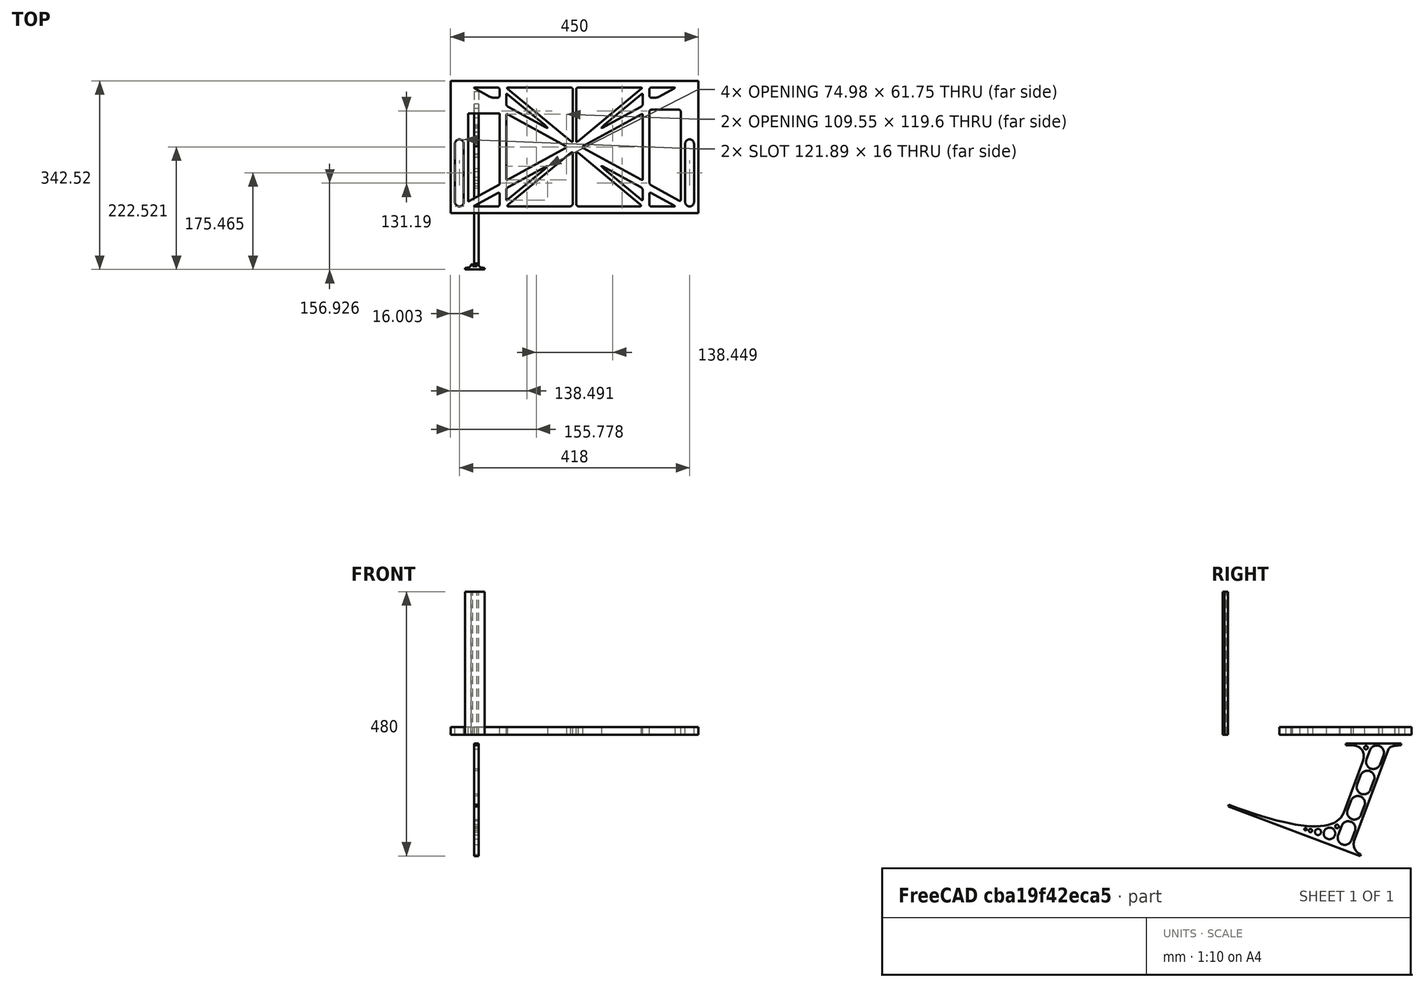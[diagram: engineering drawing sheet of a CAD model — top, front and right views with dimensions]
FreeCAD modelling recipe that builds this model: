
FCSTD DOCUMENT  (FreeCAD 0.19R0.19.2)
Label: laptopStand129FCStd
License: All rights reserved
LicenseURL: http://en.wikipedia.org/wiki/All_rights_reserved
objects: Sketcher::SketchObject×3, Part::Extrusion×3
note: 6 computed .brp shape members not serialized (recipe doc carries the construction recipe); baked Part::Feature solids carry a one-line shape summary decoded from their .brp

FEATURE [Sketcher::SketchObject] Sketch
  FullyConstrained = false
  sketch-geometry (353):
    g0: LineSegment StartX=-10.9272 StartY=-82.7794 StartZ=0 EndX=46.0728 EndY=-51.4823 EndZ=0
    g1: LineSegment StartX=-10.9272 StartY=76.4095 StartZ=0 EndX=-10.9272 EndY=-82.7794 EndZ=0
    g2: LineSegment StartX=46.0728 StartY=76.4095 StartZ=0 EndX=46.0728 EndY=-51.4823 EndZ=0
    g3: LineSegment StartX=-42.9272 StartY=136.221 StartZ=0 EndX=-42.9272 EndY=-103.779 EndZ=0
    g4: LineSegment StartX=407.073 StartY=136.221 StartZ=0 EndX=407.073 EndY=-103.779 EndZ=0
    g5: ArcOfCircle CenterX=-26.9272 CenterY=22.1087 CenterZ=0 NormalX=0 NormalY=0 NormalZ=1 AngleXU=0 Radius=8 StartAngle=1e-16 EndAngle=3.14159
    g6: ArcOfCircle CenterX=-26.9272 CenterY=-83.7794 CenterZ=0 NormalX=0 NormalY=0 NormalZ=1 AngleXU=0 Radius=8 StartAngle=3.14159 EndAngle=6.28319
    g7: LineSegment StartX=-34.9272 StartY=22.1087 StartZ=0 EndX=-34.9272 EndY=-83.7794 EndZ=0
    g8: LineSegment StartX=-18.9272 StartY=22.1087 StartZ=0 EndX=-18.9272 EndY=-83.7794 EndZ=0
    g9: ArcOfCircle CenterX=391.073 CenterY=22.1087 CenterZ=0 NormalX=0 NormalY=0 NormalZ=1 AngleXU=0 Radius=8 StartAngle=-4.4e-15 EndAngle=3.14159
    g10: LineSegment StartX=399.073 StartY=22.1087 StartZ=0 EndX=399.073 EndY=-83.7794 EndZ=0
    g11: LineSegment StartX=383.073 StartY=22.1087 StartZ=0 EndX=383.073 EndY=-83.7794 EndZ=0
    g12: ArcOfCircle CenterX=391.073 CenterY=-83.7794 CenterZ=0 NormalX=0 NormalY=0 NormalZ=1 AngleXU=0 Radius=8 StartAngle=3.14159 EndAngle=6.28319
    g13: Circle CenterX=175.022 CenterY=27.0628 CenterZ=0 NormalX=0 NormalY=0 NormalZ=1 AngleXU=0 Radius=1
    g14: Circle CenterX=179.022 CenterY=24.8665 CenterZ=0 NormalX=0 NormalY=0 NormalZ=1 AngleXU=0 Radius=1
    g15: Circle CenterX=179.022 CenterY=27.0628 CenterZ=0 NormalX=0 NormalY=0 NormalZ=1 AngleXU=0 Radius=1
    g16: BSplineCurve PolesCount=3 KnotsCount=2 Degree=2 IsPeriodic=0
    g17: GeomPoint X=175.022 Y=27.0628 Z=0
    g18: GeomPoint X=179.022 Y=27.0628 Z=0
    g19: Circle CenterX=189.124 CenterY=27.0628 CenterZ=0 NormalX=0 NormalY=0 NormalZ=1 AngleXU=0 Radius=1
    g20: Circle CenterX=185.124 CenterY=24.8665 CenterZ=0 NormalX=0 NormalY=0 NormalZ=1 AngleXU=0 Radius=1
    g21: Circle CenterX=185.124 CenterY=27.0628 CenterZ=0 NormalX=0 NormalY=0 NormalZ=1 AngleXU=0 Radius=1
    g22: BSplineCurve PolesCount=3 KnotsCount=2 Degree=2 IsPeriodic=0
    g23: GeomPoint X=189.124 Y=27.0628 Z=0
    g24: GeomPoint X=185.124 Y=27.0628 Z=0
    g25: Circle CenterX=175.022 CenterY=5.37834 CenterZ=0 NormalX=0 NormalY=0 NormalZ=1 AngleXU=0 Radius=1
    g26: Circle CenterX=179.022 CenterY=7.57463 CenterZ=0 NormalX=0 NormalY=0 NormalZ=1 AngleXU=0 Radius=1
    g27: Circle CenterX=179.022 CenterY=5.34704 CenterZ=0 NormalX=0 NormalY=0 NormalZ=1 AngleXU=0 Radius=1
    g28: BSplineCurve PolesCount=3 KnotsCount=2 Degree=2 IsPeriodic=0
    g29: GeomPoint X=175.022 Y=5.37834 Z=0
    g30: GeomPoint X=179.022 Y=5.34704 Z=0
    g31: Circle CenterX=189.124 CenterY=5.37834 CenterZ=0 NormalX=0 NormalY=0 NormalZ=1 AngleXU=0 Radius=1
    g32: Circle CenterX=185.124 CenterY=7.57463 CenterZ=0 NormalX=0 NormalY=0 NormalZ=1 AngleXU=0 Radius=1
    g33: Circle CenterX=185.124 CenterY=5.34704 CenterZ=0 NormalX=0 NormalY=0 NormalZ=1 AngleXU=0 Radius=1
    g34: BSplineCurve PolesCount=3 KnotsCount=2 Degree=2 IsPeriodic=0
    g35: GeomPoint X=189.124 Y=5.37834 Z=0
    g36: GeomPoint X=185.124 Y=5.34704 Z=0
    g37: Circle CenterX=165.871 CenterY=18.1458 CenterZ=0 NormalX=0 NormalY=0 NormalZ=1 AngleXU=0 Radius=1
    g38: Circle CenterX=169.377 CenterY=16.2206 CenterZ=0 NormalX=0 NormalY=0 NormalZ=1 AngleXU=0 Radius=1
    g39: Circle CenterX=165.871 CenterY=14.2954 CenterZ=0 NormalX=0 NormalY=0 NormalZ=1 AngleXU=0 Radius=1
    g40: BSplineCurve PolesCount=3 KnotsCount=2 Degree=2 IsPeriodic=0
    g41: GeomPoint X=165.871 Y=18.1458 Z=0
    g42: GeomPoint X=165.871 Y=14.2954 Z=0
    g43: Circle CenterX=198.275 CenterY=18.1458 CenterZ=0 NormalX=0 NormalY=0 NormalZ=1 AngleXU=0 Radius=1
    g44: Circle CenterX=194.768 CenterY=16.2206 CenterZ=0 NormalX=0 NormalY=0 NormalZ=1 AngleXU=0 Radius=1
    g45: Circle CenterX=198.275 CenterY=14.2954 CenterZ=0 NormalX=0 NormalY=0 NormalZ=1 AngleXU=0 Radius=1
    g46: BSplineCurve PolesCount=3 KnotsCount=2 Degree=2 IsPeriodic=0
    g47: GeomPoint X=198.275 Y=18.1458 Z=0
    g48: GeomPoint X=198.275 Y=14.2954 Z=0
    g49: LineSegment StartX=407.073 StartY=-103.779 StartZ=0 EndX=-42.9272 EndY=-103.779 EndZ=0
    g50: LineSegment StartX=407.073 StartY=136.221 StartZ=0 EndX=-42.9272 EndY=136.221 EndZ=0
    g51: LineSegment StartX=46.0728 StartY=76.4095 StartZ=0 EndX=-10.9272 EndY=76.4095 EndZ=0
    g52: Circle CenterX=125.607 CenterY=54.1951 CenterZ=0 NormalX=0 NormalY=0 NormalZ=1 AngleXU=0 Radius=1
    g53: Circle CenterX=139.632 CenterY=46.4944 CenterZ=0 NormalX=0 NormalY=0 NormalZ=1 AngleXU=0 Radius=1
    g54: Circle CenterX=127.326 CenterY=56.7187 CenterZ=0 NormalX=0 NormalY=0 NormalZ=1 AngleXU=0 Radius=1
    g55: BSplineCurve PolesCount=3 KnotsCount=2 Degree=2 IsPeriodic=0
    g56: GeomPoint X=125.607 Y=54.1951 Z=0
    g57: GeomPoint X=127.326 Y=56.7187 Z=0
    g58: Circle CenterX=236.821 CenterY=56.7187 CenterZ=0 NormalX=0 NormalY=0 NormalZ=1 AngleXU=0 Radius=1
    g59: Circle CenterX=224.513 CenterY=46.4944 CenterZ=0 NormalX=0 NormalY=0 NormalZ=1 AngleXU=0 Radius=1
    g60: Circle CenterX=238.538 CenterY=54.1951 CenterZ=0 NormalX=0 NormalY=0 NormalZ=1 AngleXU=0 Radius=1
    g61: BSplineCurve PolesCount=3 KnotsCount=2 Degree=2 IsPeriodic=0
    g62: GeomPoint X=236.821 Y=56.7187 Z=0
    g63: GeomPoint X=238.538 Y=54.1951 Z=0
    g64: Circle CenterX=238.538 CenterY=-21.7539 CenterZ=0 NormalX=0 NormalY=0 NormalZ=1 AngleXU=0 Radius=1
    g65: Circle CenterX=224.513 CenterY=-14.0532 CenterZ=0 NormalX=0 NormalY=0 NormalZ=1 AngleXU=0 Radius=1
    g66: Circle CenterX=236.821 CenterY=-24.2775 CenterZ=0 NormalX=0 NormalY=0 NormalZ=1 AngleXU=0 Radius=1
    g67: BSplineCurve PolesCount=3 KnotsCount=2 Degree=2 IsPeriodic=0
    g68: GeomPoint X=238.538 Y=-21.7539 Z=0
    g69: GeomPoint X=236.821 Y=-24.2775 Z=0
    g70: Circle CenterX=125.607 CenterY=-21.7539 CenterZ=0 NormalX=0 NormalY=0 NormalZ=1 AngleXU=0 Radius=1
    g71: Circle CenterX=139.632 CenterY=-14.0532 CenterZ=0 NormalX=0 NormalY=0 NormalZ=1 AngleXU=0 Radius=1
    g72: Circle CenterX=127.325 CenterY=-24.2775 CenterZ=0 NormalX=0 NormalY=0 NormalZ=1 AngleXU=0 Radius=1
    g73: BSplineCurve PolesCount=3 KnotsCount=2 Degree=2 IsPeriodic=0
    g74: GeomPoint X=125.607 Y=-21.7539 Z=0
    g75: GeomPoint X=127.325 Y=-24.2775 Z=0
    g76: Circle CenterX=302.996 CenterY=111.695 CenterZ=0 NormalX=0 NormalY=0 NormalZ=1 AngleXU=0 Radius=1
    g77: Circle CenterX=306.073 CenterY=114.251 CenterZ=0 NormalX=0 NormalY=0 NormalZ=1 AngleXU=0 Radius=1
    g78: Circle CenterX=306.073 CenterY=110.251 CenterZ=0 NormalX=0 NormalY=0 NormalZ=1 AngleXU=0 Radius=1
    g79: BSplineCurve PolesCount=3 KnotsCount=2 Degree=2 IsPeriodic=0
    g80: GeomPoint X=302.996 Y=111.695 Z=0
    g81: GeomPoint X=306.073 Y=110.251 Z=0
    g82: Circle CenterX=306.073 CenterY=95.2763 CenterZ=0 NormalX=0 NormalY=0 NormalZ=1 AngleXU=0 Radius=1
    g83: Circle CenterX=306.073 CenterY=91.2763 CenterZ=0 NormalX=0 NormalY=0 NormalZ=1 AngleXU=0 Radius=1
    g84: Circle CenterX=302.567 CenterY=89.3511 CenterZ=0 NormalX=0 NormalY=0 NormalZ=1 AngleXU=0 Radius=1
    g85: BSplineCurve PolesCount=3 KnotsCount=2 Degree=2 IsPeriodic=0
    g86: GeomPoint X=306.073 Y=95.2763 Z=0
    g87: GeomPoint X=302.567 Y=89.3511 Z=0
    g88: LineSegment StartX=306.073 StartY=110.251 StartZ=0 EndX=306.073 EndY=95.2763 EndZ=0
    g89: LineSegment StartX=302.996 StartY=111.695 StartZ=0 EndX=236.821 EndY=56.7187 EndZ=0
    g90: LineSegment StartX=238.538 StartY=54.1951 StartZ=0 EndX=302.567 EndY=89.3511 EndZ=0
    g91: Circle CenterX=61.1496 CenterY=111.695 CenterZ=0 NormalX=0 NormalY=0 NormalZ=1 AngleXU=0 Radius=1
    g92: Circle CenterX=58.0728 CenterY=114.251 CenterZ=0 NormalX=0 NormalY=0 NormalZ=1 AngleXU=0 Radius=1
    g93: Circle CenterX=58.0728 CenterY=110.251 CenterZ=0 NormalX=0 NormalY=0 NormalZ=1 AngleXU=0 Radius=1
    g94: BSplineCurve PolesCount=3 KnotsCount=2 Degree=2 IsPeriodic=0
    g95: GeomPoint X=61.1496 Y=111.695 Z=0
    g96: GeomPoint X=58.0728 Y=110.251 Z=0
    g97: Circle CenterX=61.5791 CenterY=89.3511 CenterZ=0 NormalX=0 NormalY=0 NormalZ=1 AngleXU=0 Radius=1
    g98: Circle CenterX=58.0728 CenterY=91.2763 CenterZ=0 NormalX=0 NormalY=0 NormalZ=1 AngleXU=0 Radius=1
    g99: Circle CenterX=58.0728 CenterY=95.2763 CenterZ=0 NormalX=0 NormalY=0 NormalZ=1 AngleXU=0 Radius=1
    g100: BSplineCurve PolesCount=3 KnotsCount=2 Degree=2 IsPeriodic=0
    g101: GeomPoint X=61.5791 Y=89.3511 Z=0
    g102: GeomPoint X=58.0728 Y=95.2763 Z=0
    g103: LineSegment StartX=58.0728 StartY=110.251 StartZ=0 EndX=58.0728 EndY=95.2763 EndZ=0
    g104: LineSegment StartX=61.1496 StartY=111.695 StartZ=0 EndX=127.326 EndY=56.7187 EndZ=0
    g105: LineSegment StartX=125.607 StartY=54.1951 StartZ=0 EndX=61.5791 EndY=89.3511 EndZ=0
    g106: Circle CenterX=61.5791 CenterY=-56.9099 CenterZ=0 NormalX=0 NormalY=0 NormalZ=1 AngleXU=0 Radius=1
    g107: Circle CenterX=58.0728 CenterY=-58.8351 CenterZ=0 NormalX=0 NormalY=0 NormalZ=1 AngleXU=0 Radius=1
    g108: Circle CenterX=58.0728 CenterY=-62.8351 CenterZ=0 NormalX=0 NormalY=0 NormalZ=1 AngleXU=0 Radius=1
    g109: BSplineCurve PolesCount=3 KnotsCount=2 Degree=2 IsPeriodic=0
    g110: GeomPoint X=61.5791 Y=-56.9099 Z=0
    g111: GeomPoint X=58.0728 Y=-62.8351 Z=0
    g112: Circle CenterX=58.0728 CenterY=-77.8102 CenterZ=0 NormalX=0 NormalY=0 NormalZ=1 AngleXU=0 Radius=1
    g113: Circle CenterX=58.0728 CenterY=-81.8102 CenterZ=0 NormalX=0 NormalY=0 NormalZ=1 AngleXU=0 Radius=1
    g114: Circle CenterX=61.1496 CenterY=-79.2541 CenterZ=0 NormalX=0 NormalY=0 NormalZ=1 AngleXU=0 Radius=1
    g115: BSplineCurve PolesCount=3 KnotsCount=2 Degree=2 IsPeriodic=0
    g116: GeomPoint X=58.0728 Y=-77.8102 Z=0
    g117: GeomPoint X=61.1496 Y=-79.2541 Z=0
    g118: LineSegment StartX=58.0728 StartY=-62.8351 StartZ=0 EndX=58.0728 EndY=-77.8102 EndZ=0
    g119: LineSegment StartX=61.1496 StartY=-79.2541 StartZ=0 EndX=127.325 EndY=-24.2775 EndZ=0
    g120: LineSegment StartX=125.607 StartY=-21.7539 StartZ=0 EndX=61.5791 EndY=-56.9099 EndZ=0
    g121: Circle CenterX=302.567 CenterY=-56.9099 CenterZ=0 NormalX=0 NormalY=0 NormalZ=1 AngleXU=0 Radius=1
    g122: Circle CenterX=306.073 CenterY=-58.8351 CenterZ=0 NormalX=0 NormalY=0 NormalZ=1 AngleXU=0 Radius=1
    g123: Circle CenterX=306.073 CenterY=-62.8351 CenterZ=0 NormalX=0 NormalY=0 NormalZ=1 AngleXU=0 Radius=1
    g124: BSplineCurve PolesCount=3 KnotsCount=2 Degree=2 IsPeriodic=0
    g125: GeomPoint X=302.567 Y=-56.9099 Z=0
    g126: GeomPoint X=306.073 Y=-62.8351 Z=0
    g127: Circle CenterX=302.996 CenterY=-79.2541 CenterZ=0 NormalX=0 NormalY=0 NormalZ=1 AngleXU=0 Radius=1
    g128: Circle CenterX=306.073 CenterY=-81.8102 CenterZ=0 NormalX=0 NormalY=0 NormalZ=1 AngleXU=0 Radius=1
    g129: Circle CenterX=306.073 CenterY=-77.8102 CenterZ=0 NormalX=0 NormalY=0 NormalZ=1 AngleXU=0 Radius=1
    g130: BSplineCurve PolesCount=3 KnotsCount=2 Degree=2 IsPeriodic=0
    g131: GeomPoint X=302.996 Y=-79.2541 Z=0
    g132: GeomPoint X=306.073 Y=-77.8102 Z=0
    g133: LineSegment StartX=306.073 StartY=-62.8351 StartZ=0 EndX=306.073 EndY=-77.8102 EndZ=0
    g134: LineSegment StartX=302.996 StartY=-79.2541 StartZ=0 EndX=236.821 EndY=-24.2775 EndZ=0
    g135: LineSegment StartX=238.538 StartY=-21.7539 StartZ=0 EndX=302.567 EndY=-56.9099 EndZ=0
    g136: Circle CenterX=61.6457 CenterY=-88.8112 CenterZ=0 NormalX=0 NormalY=0 NormalZ=1 AngleXU=0 Radius=1
    g137: Circle CenterX=58.0728 CenterY=-91.7794 CenterZ=0 NormalX=0 NormalY=0 NormalZ=1 AngleXU=0 Radius=1
    g138: Circle CenterX=63.9135 CenterY=-91.7794 CenterZ=0 NormalX=0 NormalY=0 NormalZ=1 AngleXU=0 Radius=1
    g139: BSplineCurve PolesCount=3 KnotsCount=2 Degree=2 IsPeriodic=0
    g140: GeomPoint X=61.6457 Y=-88.8112 Z=0
    g141: GeomPoint X=63.9135 Y=-91.7794 Z=0
    g142: Circle CenterX=179.022 CenterY=-85.8163 CenterZ=0 NormalX=0 NormalY=0 NormalZ=1 AngleXU=0 Radius=1
    g143: Circle CenterX=179.022 CenterY=-91.7794 CenterZ=0 NormalX=0 NormalY=0 NormalZ=1 AngleXU=0 Radius=1
    g144: Circle CenterX=171.895 CenterY=-91.7794 CenterZ=0 NormalX=0 NormalY=0 NormalZ=1 AngleXU=0 Radius=1
    g145: BSplineCurve PolesCount=3 KnotsCount=2 Degree=2 IsPeriodic=0
    g146: GeomPoint X=179.022 Y=-85.8163 Z=0
    g147: GeomPoint X=171.895 Y=-91.7794 Z=0
    g148: Circle CenterX=185.124 CenterY=-86.2028 CenterZ=0 NormalX=0 NormalY=0 NormalZ=1 AngleXU=0 Radius=1
    g149: Circle CenterX=185.124 CenterY=-91.7794 CenterZ=0 NormalX=0 NormalY=0 NormalZ=1 AngleXU=0 Radius=1
    g150: Circle CenterX=191.747 CenterY=-91.7794 CenterZ=0 NormalX=0 NormalY=0 NormalZ=1 AngleXU=0 Radius=1
    g151: BSplineCurve PolesCount=3 KnotsCount=2 Degree=2 IsPeriodic=0
    g152: GeomPoint X=185.124 Y=-86.2028 Z=0
    g153: GeomPoint X=191.747 Y=-91.7794 Z=0
    g154: Circle CenterX=299.888 CenterY=-86.6413 CenterZ=0 NormalX=0 NormalY=0 NormalZ=1 AngleXU=0 Radius=1
    g155: Circle CenterX=306.073 CenterY=-91.7794 CenterZ=0 NormalX=0 NormalY=0 NormalZ=1 AngleXU=0 Radius=1
    g156: Circle CenterX=298.776 CenterY=-91.7794 CenterZ=0 NormalX=0 NormalY=0 NormalZ=1 AngleXU=0 Radius=1
    g157: BSplineCurve PolesCount=3 KnotsCount=2 Degree=2 IsPeriodic=0
    g158: GeomPoint X=299.888 Y=-86.6413 Z=0
    g159: GeomPoint X=298.776 Y=-91.7794 Z=0
    g160: LineSegment StartX=189.124 StartY=5.37834 StartZ=0 EndX=299.888 EndY=-86.6413 EndZ=0
    g161: LineSegment StartX=298.776 StartY=-91.7794 StartZ=0 EndX=191.747 EndY=-91.7794 EndZ=0
    g162: LineSegment StartX=185.124 StartY=-86.2028 StartZ=0 EndX=185.124 EndY=5.34704 EndZ=0
    g163: LineSegment StartX=179.022 StartY=5.34704 StartZ=0 EndX=179.022 EndY=-85.8163 EndZ=0
    g164: LineSegment StartX=171.895 StartY=-91.7794 StartZ=0 EndX=63.9135 EndY=-91.7794 EndZ=0
    g165: LineSegment StartX=61.6457 StartY=-88.8112 StartZ=0 EndX=175.022 EndY=5.37834 EndZ=0
    g166: Circle CenterX=302.073 CenterY=124.221 CenterZ=0 NormalX=0 NormalY=0 NormalZ=1 AngleXU=0 Radius=1
    g167: Circle CenterX=306.073 CenterY=124.221 CenterZ=0 NormalX=0 NormalY=0 NormalZ=1 AngleXU=0 Radius=1
    g168: Circle CenterX=302.996 CenterY=121.665 CenterZ=0 NormalX=0 NormalY=0 NormalZ=1 AngleXU=0 Radius=1
    g169: BSplineCurve PolesCount=3 KnotsCount=2 Degree=2 IsPeriodic=0
    g170: GeomPoint X=302.073 Y=124.221 Z=0
    g171: GeomPoint X=302.996 Y=121.665 Z=0
    g172: Circle CenterX=189.124 CenterY=124.221 CenterZ=0 NormalX=0 NormalY=0 NormalZ=1 AngleXU=0 Radius=1
    g173: Circle CenterX=185.124 CenterY=124.221 CenterZ=0 NormalX=0 NormalY=0 NormalZ=1 AngleXU=0 Radius=1
    g174: Circle CenterX=185.124 CenterY=120.221 CenterZ=0 NormalX=0 NormalY=0 NormalZ=1 AngleXU=0 Radius=1
    g175: BSplineCurve PolesCount=3 KnotsCount=2 Degree=2 IsPeriodic=0
    g176: GeomPoint X=189.124 Y=124.221 Z=0
    g177: GeomPoint X=185.124 Y=120.221 Z=0
    g178: Circle CenterX=175.022 CenterY=124.221 CenterZ=0 NormalX=0 NormalY=0 NormalZ=1 AngleXU=0 Radius=1
    g179: Circle CenterX=179.022 CenterY=124.221 CenterZ=0 NormalX=0 NormalY=0 NormalZ=1 AngleXU=0 Radius=1
    g180: Circle CenterX=179.022 CenterY=120.221 CenterZ=0 NormalX=0 NormalY=0 NormalZ=1 AngleXU=0 Radius=1
    g181: BSplineCurve PolesCount=3 KnotsCount=2 Degree=2 IsPeriodic=0
    g182: GeomPoint X=175.022 Y=124.221 Z=0
    g183: GeomPoint X=179.022 Y=120.221 Z=0
    g184: Circle CenterX=62.0728 CenterY=124.221 CenterZ=0 NormalX=0 NormalY=0 NormalZ=1 AngleXU=0 Radius=1
    g185: Circle CenterX=58.0728 CenterY=124.221 CenterZ=0 NormalX=0 NormalY=0 NormalZ=1 AngleXU=0 Radius=1
    g186: Circle CenterX=61.1496 CenterY=121.665 CenterZ=0 NormalX=0 NormalY=0 NormalZ=1 AngleXU=0 Radius=1
    g187: BSplineCurve PolesCount=3 KnotsCount=2 Degree=2 IsPeriodic=0
    g188: GeomPoint X=62.0728 Y=124.221 Z=0
    g189: GeomPoint X=61.1496 Y=121.665 Z=0
    g190: LineSegment StartX=62.0728 StartY=124.221 StartZ=0 EndX=175.022 EndY=124.221 EndZ=0
    g191: LineSegment StartX=179.022 StartY=120.221 StartZ=0 EndX=179.022 EndY=27.0628 EndZ=0
    g192: LineSegment StartX=185.124 StartY=27.0628 StartZ=0 EndX=185.124 EndY=120.221 EndZ=0
    g193: LineSegment StartX=189.124 StartY=124.221 StartZ=0 EndX=302.073 EndY=124.221 EndZ=0
    g194: LineSegment StartX=302.996 StartY=121.665 StartZ=0 EndX=189.124 EndY=27.0628 EndZ=0
    g195: LineSegment StartX=175.022 StartY=27.0628 StartZ=0 EndX=61.1496 EndY=121.665 EndZ=0
    g196: Circle CenterX=61.5791 CenterY=75.4095 CenterZ=0 NormalX=0 NormalY=0 NormalZ=1 AngleXU=0 Radius=1
    g197: Circle CenterX=58.0728 CenterY=77.3346 CenterZ=0 NormalX=0 NormalY=0 NormalZ=1 AngleXU=0 Radius=1
    g198: Circle CenterX=58.0728 CenterY=73.3346 CenterZ=0 NormalX=0 NormalY=0 NormalZ=1 AngleXU=0 Radius=1
    g199: BSplineCurve PolesCount=3 KnotsCount=2 Degree=2 IsPeriodic=0
    g200: GeomPoint X=61.5791 Y=75.4095 Z=0
    g201: GeomPoint X=58.0728 Y=73.3346 Z=0
    g202: Circle CenterX=58.0728 CenterY=-40.8935 CenterZ=0 NormalX=0 NormalY=0 NormalZ=1 AngleXU=0 Radius=1
    g203: Circle CenterX=58.0728 CenterY=-44.8935 CenterZ=0 NormalX=0 NormalY=0 NormalZ=1 AngleXU=0 Radius=1
    g204: Circle CenterX=61.5791 CenterY=-42.9683 CenterZ=0 NormalX=0 NormalY=0 NormalZ=1 AngleXU=0 Radius=1
    g205: BSplineCurve PolesCount=3 KnotsCount=2 Degree=2 IsPeriodic=0
    g206: GeomPoint X=58.0728 Y=-40.8935 Z=0
    g207: GeomPoint X=61.5791 Y=-42.9683 Z=0
    g208: LineSegment StartX=61.5791 StartY=-42.9683 StartZ=0 EndX=165.871 EndY=14.2954 EndZ=0
    g209: LineSegment StartX=165.871 StartY=18.1458 StartZ=0 EndX=61.5791 EndY=75.4095 EndZ=0
    g210: LineSegment StartX=58.0728 StartY=73.3346 StartZ=0 EndX=58.0728 EndY=-40.8935 EndZ=0
    g211: Circle CenterX=302.567 CenterY=-42.9683 CenterZ=0 NormalX=0 NormalY=0 NormalZ=1 AngleXU=0 Radius=1
    g212: Circle CenterX=306.073 CenterY=-44.8935 CenterZ=0 NormalX=0 NormalY=0 NormalZ=1 AngleXU=0 Radius=1
    g213: Circle CenterX=306.073 CenterY=-40.8935 CenterZ=0 NormalX=0 NormalY=0 NormalZ=1 AngleXU=0 Radius=1
    g214: BSplineCurve PolesCount=3 KnotsCount=2 Degree=2 IsPeriodic=0
    g215: GeomPoint X=302.567 Y=-42.9683 Z=0
    g216: GeomPoint X=306.073 Y=-40.8935 Z=0
    g217: Circle CenterX=306.073 CenterY=73.3346 CenterZ=0 NormalX=0 NormalY=0 NormalZ=1 AngleXU=0 Radius=1
    g218: Circle CenterX=306.073 CenterY=77.3346 CenterZ=0 NormalX=0 NormalY=0 NormalZ=1 AngleXU=0 Radius=1
    g219: Circle CenterX=302.567 CenterY=75.4095 CenterZ=0 NormalX=0 NormalY=0 NormalZ=1 AngleXU=0 Radius=1
    g220: BSplineCurve PolesCount=3 KnotsCount=2 Degree=2 IsPeriodic=0
    g221: GeomPoint X=306.073 Y=73.3346 Z=0
    g222: GeomPoint X=302.567 Y=75.4095 Z=0
    g223: LineSegment StartX=302.567 StartY=-42.9683 StartZ=0 EndX=198.275 EndY=14.2954 EndZ=0
    g224: LineSegment StartX=198.275 StartY=18.1458 StartZ=0 EndX=302.567 EndY=75.4095 EndZ=0
    g225: LineSegment StartX=306.073 StartY=73.3346 StartZ=0 EndX=306.073 EndY=-40.8935 EndZ=0
    g226: LineSegment StartX=322.073 StartY=105.865 StartZ=0 EndX=328.643 EndY=105.865 EndZ=0
    g227: LineSegment StartX=318.073 StartY=120.221 StartZ=0 EndX=318.073 EndY=109.865 EndZ=0
    g228: LineSegment StartX=336.157 StartY=107.779 StartZ=0 EndX=362.567 EndY=122.294 EndZ=0
    g229: Circle CenterX=362.073 CenterY=124.221 CenterZ=0 NormalX=0 NormalY=0 NormalZ=1 AngleXU=0 Radius=1
    g230: Circle CenterX=366.073 CenterY=124.221 CenterZ=0 NormalX=0 NormalY=0 NormalZ=1 AngleXU=0 Radius=1
    g231: Circle CenterX=362.567 CenterY=122.294 CenterZ=0 NormalX=0 NormalY=0 NormalZ=1 AngleXU=0 Radius=1
    g232: BSplineCurve PolesCount=3 KnotsCount=2 Degree=2 IsPeriodic=0
    g233: GeomPoint X=362.073 Y=124.221 Z=0
    g234: GeomPoint X=362.567 Y=122.294 Z=0
    g235: Circle CenterX=322.073 CenterY=124.221 CenterZ=0 NormalX=0 NormalY=0 NormalZ=1 AngleXU=0 Radius=1
    g236: Circle CenterX=318.073 CenterY=124.221 CenterZ=0 NormalX=0 NormalY=0 NormalZ=1 AngleXU=0 Radius=1
    g237: Circle CenterX=318.073 CenterY=120.221 CenterZ=0 NormalX=0 NormalY=0 NormalZ=1 AngleXU=0 Radius=1
    g238: BSplineCurve PolesCount=3 KnotsCount=2 Degree=2 IsPeriodic=0
    g239: GeomPoint X=322.073 Y=124.221 Z=0
    g240: GeomPoint X=318.073 Y=120.221 Z=0
    g241: Circle CenterX=322.073 CenterY=105.865 CenterZ=0 NormalX=0 NormalY=0 NormalZ=1 AngleXU=0 Radius=1
    g242: Circle CenterX=318.073 CenterY=105.865 CenterZ=0 NormalX=0 NormalY=0 NormalZ=1 AngleXU=0 Radius=1
    g243: Circle CenterX=318.073 CenterY=109.865 CenterZ=0 NormalX=0 NormalY=0 NormalZ=1 AngleXU=0 Radius=1
    g244: BSplineCurve PolesCount=3 KnotsCount=2 Degree=2 IsPeriodic=0
    g245: GeomPoint X=322.073 Y=105.865 Z=0
    g246: GeomPoint X=318.073 Y=109.865 Z=0
    g247: Circle CenterX=336.157 CenterY=107.779 CenterZ=0 NormalX=0 NormalY=0 NormalZ=1 AngleXU=0 Radius=1
    g248: Circle CenterX=332.651 CenterY=105.853 CenterZ=0 NormalX=0 NormalY=0 NormalZ=1 AngleXU=0 Radius=1
    g249: Circle CenterX=328.643 CenterY=105.865 CenterZ=0 NormalX=0 NormalY=0 NormalZ=1 AngleXU=0 Radius=1
    g250: BSplineCurve PolesCount=3 KnotsCount=2 Degree=2 IsPeriodic=0
    g251: GeomPoint X=336.157 Y=107.779 Z=0
    g252: GeomPoint X=328.643 Y=105.865 Z=0
    g253: LineSegment StartX=322.073 StartY=124.221 StartZ=0 EndX=362.073 EndY=124.221 EndZ=0
    g254: Circle CenterX=371.567 CenterY=-80.8644 CenterZ=0 NormalX=0 NormalY=0 NormalZ=1 AngleXU=0 Radius=1
    g255: Circle CenterX=375.073 CenterY=-82.7896 CenterZ=0 NormalX=0 NormalY=0 NormalZ=1 AngleXU=0 Radius=1
    g256: Circle CenterX=375.073 CenterY=-78.7896 CenterZ=0 NormalX=0 NormalY=0 NormalZ=1 AngleXU=0 Radius=1
    g257: BSplineCurve PolesCount=3 KnotsCount=2 Degree=2 IsPeriodic=0
    g258: GeomPoint X=371.567 Y=-80.8644 Z=0
    g259: GeomPoint X=375.073 Y=-78.7896 Z=0
    g260: Circle CenterX=321.579 CenterY=-53.4075 CenterZ=0 NormalX=0 NormalY=0 NormalZ=1 AngleXU=0 Radius=1
    g261: Circle CenterX=318.073 CenterY=-51.4823 CenterZ=0 NormalX=0 NormalY=0 NormalZ=1 AngleXU=0 Radius=1
    g262: Circle CenterX=318.073 CenterY=-47.4823 CenterZ=0 NormalX=0 NormalY=0 NormalZ=1 AngleXU=0 Radius=1
    g263: BSplineCurve PolesCount=3 KnotsCount=2 Degree=2 IsPeriodic=0
    g264: GeomPoint X=321.579 Y=-53.4075 Z=0
    g265: GeomPoint X=318.073 Y=-47.4823 Z=0
    g266: Circle CenterX=318.073 CenterY=79.9235 CenterZ=0 NormalX=0 NormalY=0 NormalZ=1 AngleXU=0 Radius=1
    g267: Circle CenterX=318.073 CenterY=83.9235 CenterZ=0 NormalX=0 NormalY=0 NormalZ=1 AngleXU=0 Radius=1
    g268: Circle CenterX=322.073 CenterY=83.9235 CenterZ=0 NormalX=0 NormalY=0 NormalZ=1 AngleXU=0 Radius=1
    g269: BSplineCurve PolesCount=3 KnotsCount=2 Degree=2 IsPeriodic=0
    g270: GeomPoint X=318.073 Y=79.9235 Z=0
    g271: GeomPoint X=322.073 Y=83.9235 Z=0
    g272: Circle CenterX=375.073 CenterY=79.9235 CenterZ=0 NormalX=0 NormalY=0 NormalZ=1 AngleXU=0 Radius=1
    g273: Circle CenterX=375.073 CenterY=83.9235 CenterZ=0 NormalX=0 NormalY=0 NormalZ=1 AngleXU=0 Radius=1
    g274: Circle CenterX=371.073 CenterY=83.9235 CenterZ=0 NormalX=0 NormalY=0 NormalZ=1 AngleXU=0 Radius=1
    g275: BSplineCurve PolesCount=3 KnotsCount=2 Degree=2 IsPeriodic=0
    g276: GeomPoint X=375.073 Y=79.9235 Z=0
    g277: GeomPoint X=371.073 Y=83.9235 Z=0
    g278: LineSegment StartX=375.073 StartY=79.9235 StartZ=0 EndX=375.073 EndY=78.9235 EndZ=0
    g279: LineSegment StartX=371.567 StartY=-80.8644 StartZ=0 EndX=321.579 EndY=-53.4075 EndZ=0
    g280: LineSegment StartX=318.073 StartY=-47.4823 StartZ=0 EndX=318.073 EndY=76.4095 EndZ=0
    g281: Circle CenterX=321.579 CenterY=-67.3492 CenterZ=0 NormalX=0 NormalY=0 NormalZ=1 AngleXU=0 Radius=1
    g282: Circle CenterX=318.073 CenterY=-65.424 CenterZ=0 NormalX=0 NormalY=0 NormalZ=1 AngleXU=0 Radius=1
    g283: Circle CenterX=318.073 CenterY=-69.424 CenterZ=0 NormalX=0 NormalY=0 NormalZ=1 AngleXU=0 Radius=1
    g284: BSplineCurve PolesCount=3 KnotsCount=2 Degree=2 IsPeriodic=0
    g285: GeomPoint X=321.579 Y=-67.3492 Z=0
    g286: GeomPoint X=318.073 Y=-69.424 Z=0
    g287: Circle CenterX=362.567 CenterY=-89.8542 CenterZ=0 NormalX=0 NormalY=0 NormalZ=1 AngleXU=0 Radius=1
    g288: Circle CenterX=366.073 CenterY=-91.7794 CenterZ=0 NormalX=0 NormalY=0 NormalZ=1 AngleXU=0 Radius=1
    g289: Circle CenterX=362.073 CenterY=-91.7794 CenterZ=0 NormalX=0 NormalY=0 NormalZ=1 AngleXU=0 Radius=1
    g290: BSplineCurve PolesCount=3 KnotsCount=2 Degree=2 IsPeriodic=0
    g291: GeomPoint X=362.567 Y=-89.8542 Z=0
    g292: GeomPoint X=362.073 Y=-91.7794 Z=0
    g293: Circle CenterX=322.073 CenterY=-91.7794 CenterZ=0 NormalX=0 NormalY=0 NormalZ=1 AngleXU=0 Radius=1
    g294: Circle CenterX=318.073 CenterY=-91.7794 CenterZ=0 NormalX=0 NormalY=0 NormalZ=1 AngleXU=0 Radius=1
    g295: Circle CenterX=318.073 CenterY=-87.7794 CenterZ=0 NormalX=0 NormalY=0 NormalZ=1 AngleXU=0 Radius=1
    g296: BSplineCurve PolesCount=3 KnotsCount=2 Degree=2 IsPeriodic=0
    g297: GeomPoint X=322.073 Y=-91.7794 Z=0
    g298: GeomPoint X=318.073 Y=-87.7794 Z=0
    g299: LineSegment StartX=362.567 StartY=-89.8542 StartZ=0 EndX=321.579 EndY=-67.3492 EndZ=0
    g300: LineSegment StartX=318.073 StartY=-69.424 StartZ=0 EndX=318.073 EndY=-87.7794 EndZ=0
    g301: LineSegment StartX=322.073 StartY=-91.7794 StartZ=0 EndX=362.073 EndY=-91.7794 EndZ=0
    g302: Circle CenterX=2.07281 CenterY=124.221 CenterZ=0 NormalX=0 NormalY=0 NormalZ=1 AngleXU=0 Radius=1
    g303: Circle CenterX=1.57905 CenterY=122.295 CenterZ=0 NormalX=0 NormalY=0 NormalZ=1 AngleXU=0 Radius=1
    g304: BSplineCurve PolesCount=3 KnotsCount=2 Degree=2 IsPeriodic=0
    g305: GeomPoint X=2.07281 Y=124.221 Z=0
    g306: GeomPoint X=1.57905 Y=122.295 Z=0
    g307: Circle CenterX=42.0728 CenterY=124.221 CenterZ=0 NormalX=0 NormalY=0 NormalZ=1 AngleXU=0 Radius=1
    g308: Circle CenterX=46.0728 CenterY=124.221 CenterZ=0 NormalX=0 NormalY=0 NormalZ=1 AngleXU=0 Radius=1
    g309: Circle CenterX=46.0728 CenterY=120.221 CenterZ=0 NormalX=0 NormalY=0 NormalZ=1 AngleXU=0 Radius=1
    g310: BSplineCurve PolesCount=3 KnotsCount=2 Degree=2 IsPeriodic=0
    g311: GeomPoint X=42.0728 Y=124.221 Z=0
    g312: GeomPoint X=46.0728 Y=120.221 Z=0
    g313: Circle CenterX=46.0728 CenterY=109.865 CenterZ=0 NormalX=0 NormalY=0 NormalZ=1 AngleXU=0 Radius=1
    g314: Circle CenterX=46.0728 CenterY=105.865 CenterZ=0 NormalX=0 NormalY=0 NormalZ=1 AngleXU=0 Radius=1
    g315: Circle CenterX=42.0728 CenterY=105.865 CenterZ=0 NormalX=0 NormalY=0 NormalZ=1 AngleXU=0 Radius=1
    g316: BSplineCurve PolesCount=3 KnotsCount=2 Degree=2 IsPeriodic=0
    g317: GeomPoint X=46.0728 Y=109.865 Z=0
    g318: GeomPoint X=42.0728 Y=105.865 Z=0
    g319: Circle CenterX=35.5028 CenterY=105.865 CenterZ=0 NormalX=0 NormalY=0 NormalZ=1 AngleXU=0 Radius=1
    g320: Circle CenterX=31.5028 CenterY=105.865 CenterZ=0 NormalX=0 NormalY=0 NormalZ=1 AngleXU=0 Radius=1
    g321: Circle CenterX=27.9965 CenterY=107.79 CenterZ=0 NormalX=0 NormalY=0 NormalZ=1 AngleXU=0 Radius=1
    g322: BSplineCurve PolesCount=3 KnotsCount=2 Degree=2 IsPeriodic=0
    g323: GeomPoint X=35.5028 Y=105.865 Z=0
    g324: GeomPoint X=27.9965 Y=107.79 Z=0
    g325: LineSegment StartX=2.07281 StartY=124.221 StartZ=0 EndX=42.0728 EndY=124.221 EndZ=0
    g326: LineSegment StartX=46.0728 StartY=120.221 StartZ=0 EndX=46.0728 EndY=109.865 EndZ=0
    g327: LineSegment StartX=42.0728 StartY=105.865 StartZ=0 EndX=35.5028 EndY=105.865 EndZ=0
    g328: LineSegment StartX=27.9965 StartY=107.79 StartZ=0 EndX=1.57905 EndY=122.295 EndZ=0
    g329: Circle CenterX=42.5666 CenterY=-67.3492 CenterZ=0 NormalX=0 NormalY=0 NormalZ=1 AngleXU=0 Radius=1
    g330: Circle CenterX=46.0728 CenterY=-65.424 CenterZ=0 NormalX=0 NormalY=0 NormalZ=1 AngleXU=0 Radius=1
    g331: Circle CenterX=46.0728 CenterY=-69.424 CenterZ=0 NormalX=0 NormalY=0 NormalZ=1 AngleXU=0 Radius=1
    g332: BSplineCurve PolesCount=3 KnotsCount=2 Degree=2 IsPeriodic=0
    g333: GeomPoint X=42.5666 Y=-67.3492 Z=0
    g334: GeomPoint X=46.0728 Y=-69.424 Z=0
    g335: Circle CenterX=46.0728 CenterY=-87.7794 CenterZ=0 NormalX=0 NormalY=0 NormalZ=1 AngleXU=0 Radius=1
    g336: Circle CenterX=46.0728 CenterY=-91.7794 CenterZ=0 NormalX=0 NormalY=0 NormalZ=1 AngleXU=0 Radius=1
    g337: Circle CenterX=42.0728 CenterY=-91.7794 CenterZ=0 NormalX=0 NormalY=0 NormalZ=1 AngleXU=0 Radius=1
    g338: BSplineCurve PolesCount=3 KnotsCount=2 Degree=2 IsPeriodic=0
    g339: GeomPoint X=46.0728 Y=-87.7794 Z=0
    g340: GeomPoint X=42.0728 Y=-91.7794 Z=0
    g341: Circle CenterX=2.07281 CenterY=-91.7794 CenterZ=0 NormalX=0 NormalY=0 NormalZ=1 AngleXU=0 Radius=1
    g342: Circle CenterX=-1.92719 CenterY=-91.7794 CenterZ=0 NormalX=0 NormalY=0 NormalZ=1 AngleXU=0 Radius=1
    g343: Circle CenterX=1.57905 CenterY=-89.8542 CenterZ=0 NormalX=0 NormalY=0 NormalZ=1 AngleXU=0 Radius=1
    g344: BSplineCurve PolesCount=3 KnotsCount=2 Degree=2 IsPeriodic=0
    g345: GeomPoint X=2.07281 Y=-91.7794 Z=0
    g346: GeomPoint X=1.57905 Y=-89.8542 Z=0
    g347: LineSegment StartX=2.07281 StartY=-91.7794 StartZ=0 EndX=42.0728 EndY=-91.7794 EndZ=0
    g348: LineSegment StartX=46.0728 StartY=-87.7794 StartZ=0 EndX=46.0728 EndY=-69.424 EndZ=0
    g349: LineSegment StartX=42.5666 StartY=-67.3492 StartZ=0 EndX=1.57905 EndY=-89.8542 EndZ=0
    g350: LineSegment StartX=318.073 StartY=76.4095 StartZ=0 EndX=375.073 EndY=76.4095 EndZ=0
    g351: LineSegment StartX=375.073 StartY=76.4095 StartZ=0 EndX=375.073 EndY=-78.7896 EndZ=0
    g352: LineSegment StartX=319.162 StartY=77.4829 StartZ=0 EndX=323.162 EndY=77.4829 EndZ=0
  constraints (585):
    c: Coincident(g0,g2)
    c: Block(g0)
    c: Block(g1)
    c: Vertical(g3)
    c: Vertical(g4)
    c: Block(g4)
    c: Block(g3)
    c: Tangent(g5,g8) = 1.5708
    c: Tangent(g5,g7) = -1.5708
    c: Tangent(g7,g6) = -1.5708
    c: Tangent(g8,g6) = 1.5708
    c: Vertical(g7)
    c: Equal(g5,g6)
    c: Block(g8)
    c: Block(g7)
    c: Tangent(g9,g10) = 1.5708
    c: Tangent(g10,g12) = 1.5708
    c: Equal(g9,g12)
    c: Coincident(g11,g9)
    c: Coincident(g11,g12)
    c: Block(g10)
    c: Block(g11)
    c: Weight(g13) = 1
    c: Equal(g13,g14)
    c: Equal(g13,g15)
    c: InternalAlignment(g13,g16)
    c: InternalAlignment(g14,g16)
    c: InternalAlignment(g15,g16)
    c: InternalAlignment(g17,g16)
    c: InternalAlignment(g18,g16)
    c: Weight(g19) = 1
    c: Equal(g19,g20)
    c: Equal(g19,g21)
    c: InternalAlignment(g19,g22)
    c: InternalAlignment(g20,g22)
    c: InternalAlignment(g21,g22)
    c: InternalAlignment(g23,g22)
    c: InternalAlignment(g24,g22)
    c: Block(g22)
    c: Block(g16)
    c: Weight(g25) = 1
    c: Equal(g25,g26)
    c: Equal(g25,g27)
    c: InternalAlignment(g25,g28)
    c: InternalAlignment(g26,g28)
    c: InternalAlignment(g27,g28)
    c: InternalAlignment(g29,g28)
    c: InternalAlignment(g30,g28)
    c: Weight(g31) = 1
    c: Equal(g31,g32)
    c: Equal(g31,g33)
    c: InternalAlignment(g31,g34)
    c: InternalAlignment(g32,g34)
    c: InternalAlignment(g33,g34)
    c: InternalAlignment(g35,g34)
    c: InternalAlignment(g36,g34)
    c: Block(g34)
    c: Block(g28)
    c: Weight(g37) = 1
    c: Equal(g37,g38)
    c: Equal(g37,g39)
    c: InternalAlignment(g37,g40)
    c: InternalAlignment(g38,g40)
    c: InternalAlignment(g39,g40)
    c: InternalAlignment(g41,g40)
    c: InternalAlignment(g42,g40)
    c: Weight(g43) = 1
    c: Equal(g43,g44)
    c: Equal(g43,g45)
    c: InternalAlignment(g43,g46)
    c: InternalAlignment(g44,g46)
    c: InternalAlignment(g45,g46)
    c: InternalAlignment(g47,g46)
    c: InternalAlignment(g48,g46)
    c: Block(g40)
    c: Block(g46)
    c: Coincident(g49,g4)
    c: Coincident(g49,g3)
    c: Horizontal(g49)
    c: Distance(g49) = 450
    c: Coincident(g50,g4)
    c: Coincident(g50,g3)
    c: Horizontal(g50)
    c: Horizontal(g51)
    c: Coincident(g2,g51)
    c: Block(g51)
    c: Coincident(g1,g51)
    c: Weight(g52) = 1
    c: Equal(g52,g53)
    c: Equal(g52,g54)
    c: InternalAlignment(g52,g55)
    c: InternalAlignment(g53,g55)
    c: InternalAlignment(g54,g55)
    c: InternalAlignment(g56,g55)
    c: InternalAlignment(g57,g55)
    c: Block(g55)
    c: Weight(g58) = 1
    c: Equal(g58,g59)
    c: Equal(g58,g60)
    c: InternalAlignment(g58,g61)
    c: InternalAlignment(g59,g61)
    c: InternalAlignment(g60,g61)
    c: InternalAlignment(g62,g61)
    c: InternalAlignment(g63,g61)
    c: Block(g61)
    c: Weight(g64) = 1
    c: Equal(g64,g65)
    c: Equal(g64,g66)
    c: InternalAlignment(g64,g67)
    c: InternalAlignment(g65,g67)
    c: InternalAlignment(g66,g67)
    c: InternalAlignment(g68,g67)
    c: InternalAlignment(g69,g67)
    c: Block(g67)
    c: Weight(g70) = 1
    c: Equal(g70,g71)
    c: Equal(g70,g72)
    c: InternalAlignment(g70,g73)
    c: InternalAlignment(g71,g73)
    c: InternalAlignment(g72,g73)
    c: InternalAlignment(g74,g73)
    c: InternalAlignment(g75,g73)
    c: Block(g73)
    c: Weight(g76) = 1
    c: Equal(g76,g77)
    c: Equal(g76,g78)
    c: InternalAlignment(g76,g79)
    c: InternalAlignment(g77,g79)
    c: InternalAlignment(g78,g79)
    c: InternalAlignment(g80,g79)
    c: InternalAlignment(g81,g79)
    c: Weight(g82) = 1
    c: Equal(g82,g83)
    c: Equal(g82,g84)
    c: InternalAlignment(g82,g85)
    c: InternalAlignment(g83,g85)
    c: InternalAlignment(g84,g85)
    c: InternalAlignment(g86,g85)
    c: InternalAlignment(g87,g85)
    c: Block(g79)
    c: Block(g85)
    c: Coincident(g88,g79)
    c: Coincident(g88,g85)
    c: Vertical(g88)
    c: Coincident(g89,g79)
    c: Coincident(g89,g61)
    c: Coincident(g90,g61)
    c: Coincident(g90,g85)
    c: Weight(g91) = 1
    c: Equal(g91,g92)
    c: Equal(g91,g93)
    c: InternalAlignment(g91,g94)
    c: InternalAlignment(g92,g94)
    c: InternalAlignment(g93,g94)
    c: InternalAlignment(g95,g94)
    c: InternalAlignment(g96,g94)
    c: Weight(g97) = 1
    c: Equal(g97,g98)
    c: Equal(g97,g99)
    c: InternalAlignment(g97,g100)
    c: InternalAlignment(g98,g100)
    c: InternalAlignment(g99,g100)
    c: InternalAlignment(g101,g100)
    c: InternalAlignment(g102,g100)
    c: Block(g94)
    c: Block(g100)
    c: Coincident(g103,g94)
    c: Coincident(g103,g100)
    c: Vertical(g103)
    c: Coincident(g104,g94)
    c: Coincident(g104,g55)
    c: Coincident(g105,g55)
    c: Coincident(g105,g100)
    c: Weight(g106) = 1
    c: Equal(g106,g107)
    c: Equal(g106,g108)
    c: InternalAlignment(g106,g109)
    c: InternalAlignment(g107,g109)
    c: InternalAlignment(g108,g109)
    c: InternalAlignment(g110,g109)
    c: InternalAlignment(g111,g109)
    c: Weight(g112) = 1
    c: Equal(g112,g113)
    c: Equal(g112,g114)
    c: InternalAlignment(g112,g115)
    c: InternalAlignment(g113,g115)
    c: InternalAlignment(g114,g115)
    c: InternalAlignment(g116,g115)
    c: InternalAlignment(g117,g115)
    c: Block(g109)
    c: Block(g115)
    c: Coincident(g118,g109)
    c: Coincident(g118,g115)
    c: Vertical(g118)
    c: Coincident(g119,g115)
    c: Coincident(g119,g73)
    c: Coincident(g120,g73)
    c: Coincident(g120,g109)
    c: Weight(g121) = 1
    c: Equal(g121,g122)
    c: Equal(g121,g123)
    c: InternalAlignment(g121,g124)
    c: InternalAlignment(g122,g124)
    c: InternalAlignment(g123,g124)
    c: InternalAlignment(g125,g124)
    c: InternalAlignment(g126,g124)
    c: Weight(g127) = 1
    c: Equal(g127,g128)
    c: Equal(g127,g129)
    c: InternalAlignment(g127,g130)
    c: InternalAlignment(g128,g130)
    c: InternalAlignment(g129,g130)
    c: InternalAlignment(g131,g130)
    c: InternalAlignment(g132,g130)
    c: Block(g124)
    c: Block(g130)
    c: Coincident(g133,g124)
    c: Coincident(g133,g130)
    c: Vertical(g133)
    c: Coincident(g134,g130)
    c: Coincident(g134,g67)
    c: Coincident(g135,g67)
    c: Coincident(g135,g124)
    c: Weight(g136) = 1
    c: Equal(g136,g137)
    c: Equal(g136,g138)
    c: InternalAlignment(g136,g139)
    c: InternalAlignment(g137,g139)
    c: InternalAlignment(g138,g139)
    c: InternalAlignment(g140,g139)
    c: InternalAlignment(g141,g139)
    c: Weight(g142) = 1
    c: Equal(g142,g143)
    c: Equal(g142,g144)
    c: InternalAlignment(g142,g145)
    c: InternalAlignment(g143,g145)
    c: InternalAlignment(g144,g145)
    c: InternalAlignment(g146,g145)
    c: InternalAlignment(g147,g145)
    c: Weight(g148) = 1
    c: Equal(g148,g149)
    c: Equal(g148,g150)
    c: InternalAlignment(g148,g151)
    c: InternalAlignment(g149,g151)
    c: InternalAlignment(g150,g151)
    c: InternalAlignment(g152,g151)
    c: InternalAlignment(g153,g151)
    c: Weight(g154) = 1
    c: Equal(g154,g155)
    c: Equal(g154,g156)
    c: InternalAlignment(g154,g157)
    c: InternalAlignment(g155,g157)
    c: InternalAlignment(g156,g157)
    c: InternalAlignment(g158,g157)
    c: InternalAlignment(g159,g157)
    c: Block(g157)
    c: Block(g151)
    c: Block(g145)
    c: Block(g139)
    c: Coincident(g160,g34)
    c: Coincident(g160,g157)
    c: Coincident(g161,g157)
    c: Coincident(g161,g151)
    c: Horizontal(g161)
    c: Coincident(g162,g151)
    c: Coincident(g162,g34)
    c: Vertical(g162)
    c: Coincident(g163,g28)
    c: Coincident(g163,g145)
    c: Vertical(g163)
    c: Coincident(g164,g145)
    c: Coincident(g164,g139)
    c: Horizontal(g164)
    c: Coincident(g165,g139)
    c: Coincident(g165,g28)
    c: Weight(g166) = 1
    c: Equal(g166,g167)
    c: Equal(g166,g168)
    c: InternalAlignment(g166,g169)
    c: InternalAlignment(g167,g169)
    c: InternalAlignment(g168,g169)
    c: InternalAlignment(g170,g169)
    c: InternalAlignment(g171,g169)
    c: Weight(g172) = 1
    c: Equal(g172,g173)
    c: Equal(g172,g174)
    c: InternalAlignment(g172,g175)
    c: InternalAlignment(g173,g175)
    c: InternalAlignment(g174,g175)
    c: InternalAlignment(g176,g175)
    c: InternalAlignment(g177,g175)
    c: Weight(g178) = 1
    c: Equal(g178,g179)
    c: Equal(g178,g180)
    c: InternalAlignment(g178,g181)
    c: InternalAlignment(g179,g181)
    c: InternalAlignment(g180,g181)
    c: InternalAlignment(g182,g181)
    c: InternalAlignment(g183,g181)
    c: Weight(g184) = 1
    c: Equal(g184,g185)
    c: Equal(g184,g186)
    c: InternalAlignment(g184,g187)
    c: InternalAlignment(g185,g187)
    c: InternalAlignment(g186,g187)
    c: InternalAlignment(g188,g187)
    c: InternalAlignment(g189,g187)
    c: Block(g187)
    c: Block(g181)
    c: Block(g175)
    c: Block(g169)
    c: Coincident(g190,g187)
    c: Coincident(g190,g181)
    c: Horizontal(g190)
    c: Coincident(g191,g181)
    c: Coincident(g191,g16)
    c: Vertical(g191)
    c: Coincident(g192,g22)
    c: Coincident(g192,g175)
    c: Vertical(g192)
    c: Coincident(g193,g175)
    c: Coincident(g193,g169)
    c: Horizontal(g193)
    c: Coincident(g194,g169)
    c: Coincident(g194,g22)
    c: Coincident(g195,g16)
    c: Weight(g196) = 1
    c: Equal(g196,g197)
    c: Equal(g196,g198)
    c: InternalAlignment(g196,g199)
    c: InternalAlignment(g197,g199)
    c: InternalAlignment(g198,g199)
    c: InternalAlignment(g200,g199)
    c: InternalAlignment(g201,g199)
    c: Weight(g202) = 1
    c: Equal(g202,g203)
    c: Equal(g202,g204)
    c: InternalAlignment(g202,g205)
    c: InternalAlignment(g203,g205)
    c: InternalAlignment(g204,g205)
    c: InternalAlignment(g206,g205)
    c: InternalAlignment(g207,g205)
    c: Block(g205)
    c: Block(g199)
    c: Coincident(g208,g205)
    c: Coincident(g208,g40)
    c: Coincident(g209,g40)
    c: Coincident(g209,g199)
    c: Coincident(g210,g199)
    c: Coincident(g210,g205)
    c: Vertical(g210)
    c: Weight(g211) = 1
    c: Equal(g211,g212)
    c: Equal(g211,g213)
    c: InternalAlignment(g211,g214)
    c: InternalAlignment(g212,g214)
    c: InternalAlignment(g213,g214)
    c: InternalAlignment(g215,g214)
    c: InternalAlignment(g216,g214)
    c: Weight(g217) = 1
    c: Equal(g217,g218)
    c: Equal(g217,g219)
    c: InternalAlignment(g217,g220)
    c: InternalAlignment(g218,g220)
    c: InternalAlignment(g219,g220)
    c: InternalAlignment(g221,g220)
    c: InternalAlignment(g222,g220)
    c: Block(g220)
    c: Block(g214)
    c: Coincident(g223,g214)
    c: Coincident(g223,g46)
    c: Coincident(g224,g46)
    c: Coincident(g224,g220)
    c: Coincident(g225,g220)
    c: Coincident(g225,g214)
    c: Vertical(g225)
    c: Horizontal(g226)
    c: Block(g226)
    c: Vertical(g227)
    c: Block(g227)
    c: Block(g228)
    c: Weight(g229) = 1
    c: Equal(g229,g230)
    c: Equal(g229,g231)
    c: InternalAlignment(g229,g232)
    c: InternalAlignment(g230,g232)
    c: InternalAlignment(g231,g232)
    c: InternalAlignment(g233,g232)
    c: InternalAlignment(g234,g232)
    c: Weight(g235) = 1
    c: Equal(g235,g236)
    c: Equal(g235,g237)
    c: InternalAlignment(g235,g238)
    c: InternalAlignment(g236,g238)
    c: InternalAlignment(g237,g238)
    c: InternalAlignment(g239,g238)
    c: InternalAlignment(g240,g238)
    c: Weight(g241) = 1
    c: Equal(g241,g242)
    c: Equal(g241,g243)
    c: InternalAlignment(g241,g244)
    c: InternalAlignment(g242,g244)
    c: InternalAlignment(g243,g244)
    c: InternalAlignment(g245,g244)
    c: InternalAlignment(g246,g244)
    c: Weight(g247) = 1
    c: Equal(g247,g248)
    c: Equal(g247,g249)
    c: InternalAlignment(g247,g250)
    c: InternalAlignment(g248,g250)
    c: InternalAlignment(g249,g250)
    c: InternalAlignment(g251,g250)
    c: InternalAlignment(g252,g250)
    c: Block(g232)
    c: Block(g238)
    c: Block(g244)
    c: Block(g250)
    c: Coincident(g253,g238)
    c: Coincident(g253,g232)
    c: Horizontal(g253)
    c: Block(g195)
    c: Weight(g254) = 1
    c: Equal(g254,g255)
    c: Equal(g254,g256)
    c: InternalAlignment(g254,g257)
    c: InternalAlignment(g255,g257)
    c: InternalAlignment(g256,g257)
    c: InternalAlignment(g258,g257)
    c: InternalAlignment(g259,g257)
    c: Weight(g260) = 1
    c: Equal(g260,g261)
    c: Equal(g260,g262)
    c: InternalAlignment(g260,g263)
    c: InternalAlignment(g261,g263)
    c: InternalAlignment(g262,g263)
    c: InternalAlignment(g264,g263)
    c: InternalAlignment(g265,g263)
    c: Weight(g266) = 1
    c: Equal(g266,g267)
    c: Equal(g266,g268)
    c: InternalAlignment(g266,g269)
    c: InternalAlignment(g267,g269)
    c: InternalAlignment(g268,g269)
    c: InternalAlignment(g270,g269)
    c: InternalAlignment(g271,g269)
    c: Weight(g272) = 1
    c: Equal(g272,g273)
    c: Equal(g272,g274)
    c: InternalAlignment(g272,g275)
    c: InternalAlignment(g273,g275)
    c: InternalAlignment(g274,g275)
    c: InternalAlignment(g276,g275)
    c: InternalAlignment(g277,g275)
    c: Block(g257)
    c: Block(g263)
    c: Block(g269)
    c: Block(g275)
    c: Coincident(g278,g275)
    c: Coincident(g351,g257)
    c: Vertical(g278)
    c: Coincident(g279,g257)
    c: Coincident(g279,g263)
    c: Coincident(g280,g263)
    c: Vertical(g280)
    c: Weight(g281) = 1
    c: Equal(g281,g282)
    c: Equal(g281,g283)
    c: InternalAlignment(g281,g284)
    c: InternalAlignment(g282,g284)
    c: InternalAlignment(g283,g284)
    c: InternalAlignment(g285,g284)
    c: InternalAlignment(g286,g284)
    c: Weight(g287) = 1
    c: Equal(g287,g288)
    c: Equal(g287,g289)
    c: InternalAlignment(g287,g290)
    c: InternalAlignment(g288,g290)
    c: InternalAlignment(g289,g290)
    c: InternalAlignment(g291,g290)
    c: InternalAlignment(g292,g290)
    c: Weight(g293) = 1
    c: Equal(g293,g294)
    c: Equal(g293,g295)
    c: InternalAlignment(g293,g296)
    c: InternalAlignment(g294,g296)
    c: InternalAlignment(g295,g296)
    c: InternalAlignment(g297,g296)
    c: InternalAlignment(g298,g296)
    c: Block(g296)
    c: Block(g290)
    c: Block(g284)
    c: Coincident(g299,g290)
    c: Coincident(g299,g284)
    c: Coincident(g300,g284)
    c: Coincident(g300,g296)
    c: Vertical(g300)
    c: Coincident(g301,g296)
    c: Coincident(g301,g290)
    c: Horizontal(g301)
    c: Weight(g302) = 1
    c: Equal(g302,g303)
    c: InternalAlignment(g302,g304)
    c: InternalAlignment(g303,g304)
    c: InternalAlignment(g305,g304)
    c: InternalAlignment(g306,g304)
    c: Weight(g307) = 1
    c: Equal(g307,g308)
    c: Equal(g307,g309)
    c: InternalAlignment(g307,g310)
    c: InternalAlignment(g308,g310)
    c: InternalAlignment(g309,g310)
    c: InternalAlignment(g311,g310)
    c: InternalAlignment(g312,g310)
    c: Weight(g313) = 1
    c: Equal(g313,g314)
    c: Equal(g313,g315)
    c: InternalAlignment(g313,g316)
    c: InternalAlignment(g314,g316)
    c: InternalAlignment(g315,g316)
    c: InternalAlignment(g317,g316)
    c: InternalAlignment(g318,g316)
    c: Equal(g319,g320)
    c: Equal(g319,g321)
    c: InternalAlignment(g319,g322)
    c: InternalAlignment(g320,g322)
    c: InternalAlignment(g321,g322)
    c: InternalAlignment(g323,g322)
    c: InternalAlignment(g324,g322)
    c: Block(g310)
    c: Block(g316)
    c: Block(g322)
    c: Block(g304)
    c: Coincident(g325,g304)
    c: Coincident(g325,g310)
    c: Horizontal(g325)
    c: Coincident(g326,g310)
    c: Coincident(g326,g316)
    c: Vertical(g326)
    c: Coincident(g327,g316)
    c: Coincident(g327,g322)
    c: Horizontal(g327)
    c: Coincident(g328,g322)
    c: Coincident(g328,g304)
    c: Weight(g329) = 1
    c: Equal(g329,g330)
    c: Equal(g329,g331)
    c: InternalAlignment(g329,g332)
    c: InternalAlignment(g330,g332)
    c: InternalAlignment(g331,g332)
    c: InternalAlignment(g333,g332)
    c: InternalAlignment(g334,g332)
    c: Weight(g335) = 1
    c: Equal(g335,g336)
    c: Equal(g335,g337)
    c: InternalAlignment(g335,g338)
    c: InternalAlignment(g336,g338)
    c: InternalAlignment(g337,g338)
    c: InternalAlignment(g339,g338)
    c: InternalAlignment(g340,g338)
    c: Weight(g341) = 1
    c: Equal(g341,g342)
    c: Equal(g341,g343)
    c: InternalAlignment(g341,g344)
    c: InternalAlignment(g342,g344)
    c: InternalAlignment(g343,g344)
    c: InternalAlignment(g345,g344)
    c: InternalAlignment(g346,g344)
    c: Block(g344)
    c: Block(g338)
    c: Block(g332)
    c: Coincident(g347,g344)
    c: Coincident(g347,g338)
    c: Horizontal(g347)
    c: Coincident(g348,g338)
    c: Coincident(g348,g332)
    c: Vertical(g348)
    c: Coincident(g349,g332)
    c: Coincident(g349,g344)
    c: Block(g350)
    c: PointOnObject(g278,g272)
    c: Coincident(g351,g350)
    c: Tangent(g278,g351)
    c: Coincident(g280,g350)
    c: Horizontal(g352)
    c: Distance(g352) = 4
FEATURE [Sketcher::SketchObject] Sketch001
  FullyConstrained = true
  MapMode = 4
  Placement = pos=(0,0,0) rot=(0.57735,0.57735,0.57735;2.0944rad)
  Support = -> [Sketch]
  sketch-geometry (46):
    g0: BSplineCurve PolesCount=3 KnotsCount=2 Degree=2 IsPeriodic=0
    g1: ArcOfCircle CenterX=73.1223 CenterY=-32.291 CenterZ=0 NormalX=0 NormalY=0 NormalZ=1 AngleXU=0 Radius=13 StartAngle=5.92268 EndAngle=9.06428
    g2: ArcOfCircle CenterX=66.7816 CenterY=-49.1439 CenterZ=0 NormalX=0 NormalY=0 NormalZ=1 AngleXU=0 Radius=13 StartAngle=2.78068 EndAngle=5.92131
    g3: ArcOfCircle CenterX=55.9263 CenterY=-78.1807 CenterZ=0 NormalX=0 NormalY=0 NormalZ=1 AngleXU=0 Radius=13 StartAngle=5.92268 EndAngle=9.06428
    g4: ArcOfCircle CenterX=49.5884 CenterY=-95.0342 CenterZ=0 NormalX=0 NormalY=0 NormalZ=1 AngleXU=0 Radius=13 StartAngle=2.78068 EndAngle=5.92131
    g5: ArcOfCircle CenterX=38.7206 CenterY=-124.067 CenterZ=0 NormalX=0 NormalY=0 NormalZ=1 AngleXU=0 Radius=13 StartAngle=5.92268 EndAngle=9.06428
    g6: ArcOfCircle CenterX=32.3875 CenterY=-140.92 CenterZ=0 NormalX=0 NormalY=0 NormalZ=1 AngleXU=0 Radius=13 StartAngle=2.78068 EndAngle=5.92131
    g7: ArcOfCircle CenterX=21.4715 CenterY=-169.934 CenterZ=0 NormalX=0 NormalY=0 NormalZ=1 AngleXU=0 Radius=13 StartAngle=5.92268 EndAngle=9.06428
    g8: ArcOfCircle CenterX=15.1336 CenterY=-186.787 CenterZ=0 NormalX=0 NormalY=0 NormalZ=1 AngleXU=0 Radius=13 StartAngle=2.78068 EndAngle=5.92131
    g9-g12: Circle x4 (B-spline internal-alignment scaffolding for g13; pole/knot coordinates omitted)
    g13: BSplineCurve PolesCount=4 KnotsCount=2 Degree=3 IsPeriodic=0
    g14: GeomPoint X=28.8094 Y=-19.0875 Z=0
    g15: GeomPoint X=47.0443 Y=-50.4712 Z=0
    g16: Circle CenterX=53.5586 CenterY=-23.2695 CenterZ=0 NormalX=0 NormalY=0 NormalZ=1 AngleXU=0 Radius=3.24518
    g17: Circle CenterX=-195.441 CenterY=-127.082 CenterZ=0 NormalX=0 NormalY=0 NormalZ=1 AngleXU=0 Radius=1
    g18: Circle CenterX=-8.24091 CenterY=-197.481 CenterZ=0 NormalX=0 NormalY=0 NormalZ=1 AngleXU=0 Radius=1
    g19: Circle CenterX=12.8789 CenterY=-141.321 CenterZ=0 NormalX=0 NormalY=0 NormalZ=1 AngleXU=0 Radius=1
    g20: BSplineCurve PolesCount=3 KnotsCount=2 Degree=2 IsPeriodic=0
    g21: GeomPoint X=-195.441 Y=-127.082 Z=0
    g22: GeomPoint X=12.8789 Y=-141.321 Z=0
    g23: Circle CenterX=-12.8016 CenterY=-179.036 CenterZ=0 NormalX=0 NormalY=0 NormalZ=1 AngleXU=0 Radius=10.5072
    g24: Circle CenterX=0.933922 CenterY=-166.43 CenterZ=0 NormalX=0 NormalY=0 NormalZ=1 AngleXU=0 Radius=3.26661
    g25: Circle CenterX=-33.5518 CenterY=-176.44 CenterZ=0 NormalX=0 NormalY=0 NormalZ=1 AngleXU=0 Radius=5.64388
    g26: Circle CenterX=-47.2366 CenterY=-173.859 CenterZ=0 NormalX=0 NormalY=0 NormalZ=1 AngleXU=0 Radius=3.01653
    g27: Circle CenterX=-56.2595 CenterY=-171.456 CenterZ=0 NormalX=0 NormalY=0 NormalZ=1 AngleXU=0 Radius=2.12826
    g28: ArcOfCircle CenterX=51.2151 CenterY=-198.473 CenterZ=0 NormalX=0 NormalY=0 NormalZ=1 AngleXU=0 Radius=20 StartAngle=2.78189 EndAngle=4.35269
    g29: LineSegment StartX=32.4951 StartY=-191.433 StartZ=0 EndX=94.6578 EndY=-26.1352 EndZ=0
    g30: LineSegment StartX=43.1192 StartY=-220.001 StartZ=0 EndX=-196.497 EndY=-129.89 EndZ=0
    g31: LineSegment StartX=43.1192 StartY=-220.001 StartZ=0 EndX=44.1752 EndY=-217.193 EndZ=0
    g32: LineSegment StartX=117.223 StartY=-19.0875 StartZ=0 EndX=117.223 EndY=-16.0875 EndZ=0
    g33: LineSegment StartX=117.223 StartY=-16.0875 StartZ=0 EndX=17.2232 EndY=-16.0875 EndZ=0
    g34: LineSegment StartX=17.2232 StartY=-16.0875 StartZ=0 EndX=17.2232 EndY=-19.0875 EndZ=0
    g35: LineSegment StartX=28.8094 StartY=-19.0875 StartZ=0 EndX=17.2232 EndY=-19.0875 EndZ=0
    g36: LineSegment StartX=47.0443 StartY=-50.4712 StartZ=0 EndX=12.8789 EndY=-141.321 EndZ=0
    g37: LineSegment StartX=-195.441 StartY=-127.082 StartZ=0 EndX=-196.497 EndY=-129.89 EndZ=0
    g38: LineSegment StartX=85.2866 StartY=-36.8766 StartZ=0 EndX=78.9396 EndY=-53.7463 EndZ=0
    g39: LineSegment StartX=60.9579 StartY=-27.7053 StartZ=0 EndX=54.6191 EndY=-44.5532 EndZ=0
    g40: LineSegment StartX=68.0907 StartY=-82.7664 StartZ=0 EndX=61.7465 EndY=-99.6365 EndZ=0
    g41: LineSegment StartX=43.7619 StartY=-73.595 StartZ=0 EndX=37.426 EndY=-90.4435 EndZ=0
    g42: LineSegment StartX=50.885 StartY=-128.652 StartZ=0 EndX=44.5456 EndY=-145.522 EndZ=0
    g43: LineSegment StartX=26.5562 StartY=-119.481 StartZ=0 EndX=20.2251 EndY=-136.329 EndZ=0
    g44: LineSegment StartX=9.3071 StartY=-165.349 StartZ=0 EndX=2.97115 EndY=-182.197 EndZ=0
    g45: LineSegment StartX=33.6358 StartY=-174.52 StartZ=0 EndX=27.2917 EndY=-191.39 EndZ=0
  constraints (71):
    c: Block(g0)
    c: Block(g1)
    c: Block(g2)
    c: Block(g4)
    c: Block(g3)
    c: Block(g6)
    c: Block(g5)
    c: Block(g8)
    c: Block(g7)
    c: Weight(g9) = 1
    c: Equal(g9,g10)
    c: Equal(g9,g11)
    c: Equal(g9,g12)
    c: InternalAlignment(g9-g12 -> g13) x4
    c: InternalAlignment(g14,g13)
    c: InternalAlignment(g15,g13)
    c: Block(g16)
    c: Weight(g17) = 1
    c: Equal(g17,g18)
    c: Equal(g17,g19)
    c: InternalAlignment(g17,g20)
    c: InternalAlignment(g18,g20)
    c: InternalAlignment(g19,g20)
    c: InternalAlignment(g21,g20)
    c: InternalAlignment(g22,g20)
    c: Block(g20)
    c: Block(g23)
    c: Block(g24)
    c: Block(g25)
    c: Block(g26)
    c: Block(g27)
    c: Block(g28)
    c: Coincident(g29,g28)
    c: Coincident(g29,g0)
    c: Block(g13)
    c: Coincident(g31,g30)
    c: Coincident(g31,g28)
    c: Block(g31)
    c: Coincident(g32,g0)
    c: Vertical(g32)
    c: Coincident(g33,g32)
    c: Horizontal(g33)
    c: Coincident(g34,g33)
    c: Vertical(g34)
    c: Block(g33)
    c: Coincident(g35,g13)
    c: Coincident(g35,g34)
    c: Horizontal(g35)
    c: Coincident(g36,g13)
    c: Coincident(g36,g20)
    c: Coincident(g37,g20)
    c: Coincident(g37,g30)
    c: Block(g30)
    c: Coincident(g38,g1)
    c: Coincident(g38,g2)
    c: Coincident(g39,g1)
    c: Coincident(g39,g2)
    c: Coincident(g40,g3)
    c: Coincident(g40,g4)
    c: Coincident(g41,g3)
    c: Coincident(g41,g4)
    c: Coincident(g42,g5)
    c: Coincident(g42,g6)
    c: Coincident(g43,g5)
    c: Coincident(g43,g6)
    c: Coincident(g44,g7)
    c: Coincident(g44,g8)
    c: Coincident(g45,g7)
    c: Coincident(g45,g8)
    c: Distance(g30) = 256
    c: Distance(g33) = 100
FEATURE [Part::Extrusion] Extrude002
  Base = -> Sketch001
  Dir = (1,0,0)
  DirMode = 2
  FaceMakerClass = Part::FaceMakerBullseye
  LengthFwd = 8
  LengthRev = 0
  Solid = true
  Symmetric = false
FEATURE [Sketcher::SketchObject] Sketch002
  FullyConstrained = true
  sketch-geometry (20):
    g0: LineSegment StartX=-2.77179 StartY=-200.304 StartZ=0 EndX=5.22821 EndY=-200.304 EndZ=0
    g1: LineSegment StartX=5.22821 StartY=-200.304 StartZ=0 EndX=5.22821 EndY=-197.304 EndZ=0
    g2: LineSegment StartX=-2.77179 StartY=-200.304 StartZ=0 EndX=-2.77179 EndY=-197.304 EndZ=0
    g3: LineSegment StartX=5.22821 StartY=-197.304 StartZ=0 EndX=8.22821 EndY=-197.304 EndZ=0
    g4: LineSegment StartX=-2.77179 StartY=-197.304 StartZ=0 EndX=-5.77179 EndY=-197.304 EndZ=0
    g5: LineSegment StartX=19.2282 StartY=-203.304 StartZ=0 EndX=19.2282 EndY=-206.304 EndZ=0
    g6: LineSegment StartX=-16.7718 StartY=-203.304 StartZ=0 EndX=-16.7718 EndY=-206.304 EndZ=0
    g7: LineSegment StartX=-16.7718 StartY=-206.304 StartZ=0 EndX=19.2282 EndY=-206.304 EndZ=0
    g8: Circle CenterX=-16.7718 CenterY=-203.304 CenterZ=0 NormalX=0 NormalY=0 NormalZ=1 AngleXU=0 Radius=1
    g9: Circle CenterX=-5.77179 CenterY=-203.304 CenterZ=0 NormalX=0 NormalY=0 NormalZ=1 AngleXU=0 Radius=1
    g10: Circle CenterX=-5.77179 CenterY=-197.304 CenterZ=0 NormalX=0 NormalY=0 NormalZ=1 AngleXU=0 Radius=1
    g11: BSplineCurve PolesCount=3 KnotsCount=2 Degree=2 IsPeriodic=0
    g12: GeomPoint X=-16.7718 Y=-203.304 Z=0
    g13: GeomPoint X=-5.77179 Y=-197.304 Z=0
    g14: Circle CenterX=19.2282 CenterY=-203.304 CenterZ=0 NormalX=0 NormalY=0 NormalZ=1 AngleXU=0 Radius=1
    g15: Circle CenterX=8.22821 CenterY=-203.304 CenterZ=0 NormalX=0 NormalY=0 NormalZ=1 AngleXU=0 Radius=1
    g16: Circle CenterX=8.22821 CenterY=-197.304 CenterZ=0 NormalX=0 NormalY=0 NormalZ=1 AngleXU=0 Radius=1
    g17: BSplineCurve PolesCount=3 KnotsCount=2 Degree=2 IsPeriodic=0
    g18: GeomPoint X=19.2282 Y=-203.304 Z=0
    g19: GeomPoint X=8.22821 Y=-197.304 Z=0
  constraints (41):
    c: Horizontal(g0)
    c: Distance(g0) = 8
    c: Coincident(g1,g0)
    c: Vertical(g1)
    c: Distance(g1) = 3
    c: Coincident(g2,g0)
    c: Vertical(g2)
    c: Distance(g2) = 3
    c: Coincident(g3,g1)
    c: Horizontal(g3)
    c: Distance(g3) = 3
    c: Coincident(g4,g2)
    c: Horizontal(g4)
    c: Distance(g4) = 3
    c: Vertical(g5)
    c: Vertical(g6)
    c: Coincident(g7,g6)
    c: Coincident(g7,g5)
    c: Weight(g8) = 1
    c: Equal(g8,g9)
    c: Equal(g8,g10)
    c: Coincident(g11,g4)
    c: InternalAlignment(g8,g11)
    c: InternalAlignment(g9,g11)
    c: InternalAlignment(g10,g11)
    c: InternalAlignment(g12,g11)
    c: InternalAlignment(g13,g11)
    c: Coincident(g17,g5)
    c: Weight(g14) = 1
    c: Equal(g14,g15)
    c: Equal(g14,g16)
    c: Coincident(g17,g3)
    c: InternalAlignment(g14,g17)
    c: InternalAlignment(g15,g17)
    c: InternalAlignment(g16,g17)
    c: InternalAlignment(g18,g17)
    c: InternalAlignment(g19,g17)
    c: Block(g7)
    c: Block(g17)
    c: Block(g11)
    c: Block(g6)
FEATURE [Part::Extrusion] Extrude003
  Base = -> Sketch002
  Dir = (0,0,1)
  DirMode = 2
  FaceMakerClass = Part::FaceMakerBullseye
  LengthFwd = 260
  LengthRev = 0
  Solid = true
  Symmetric = false
FEATURE [Part::Extrusion] Extrude
  Base = -> Sketch
  Dir = (0,0,1)
  DirMode = 2
  FaceMakerClass = Part::FaceMakerBullseye
  LengthFwd = 14
  LengthRev = 0
  Solid = true
  Symmetric = false
